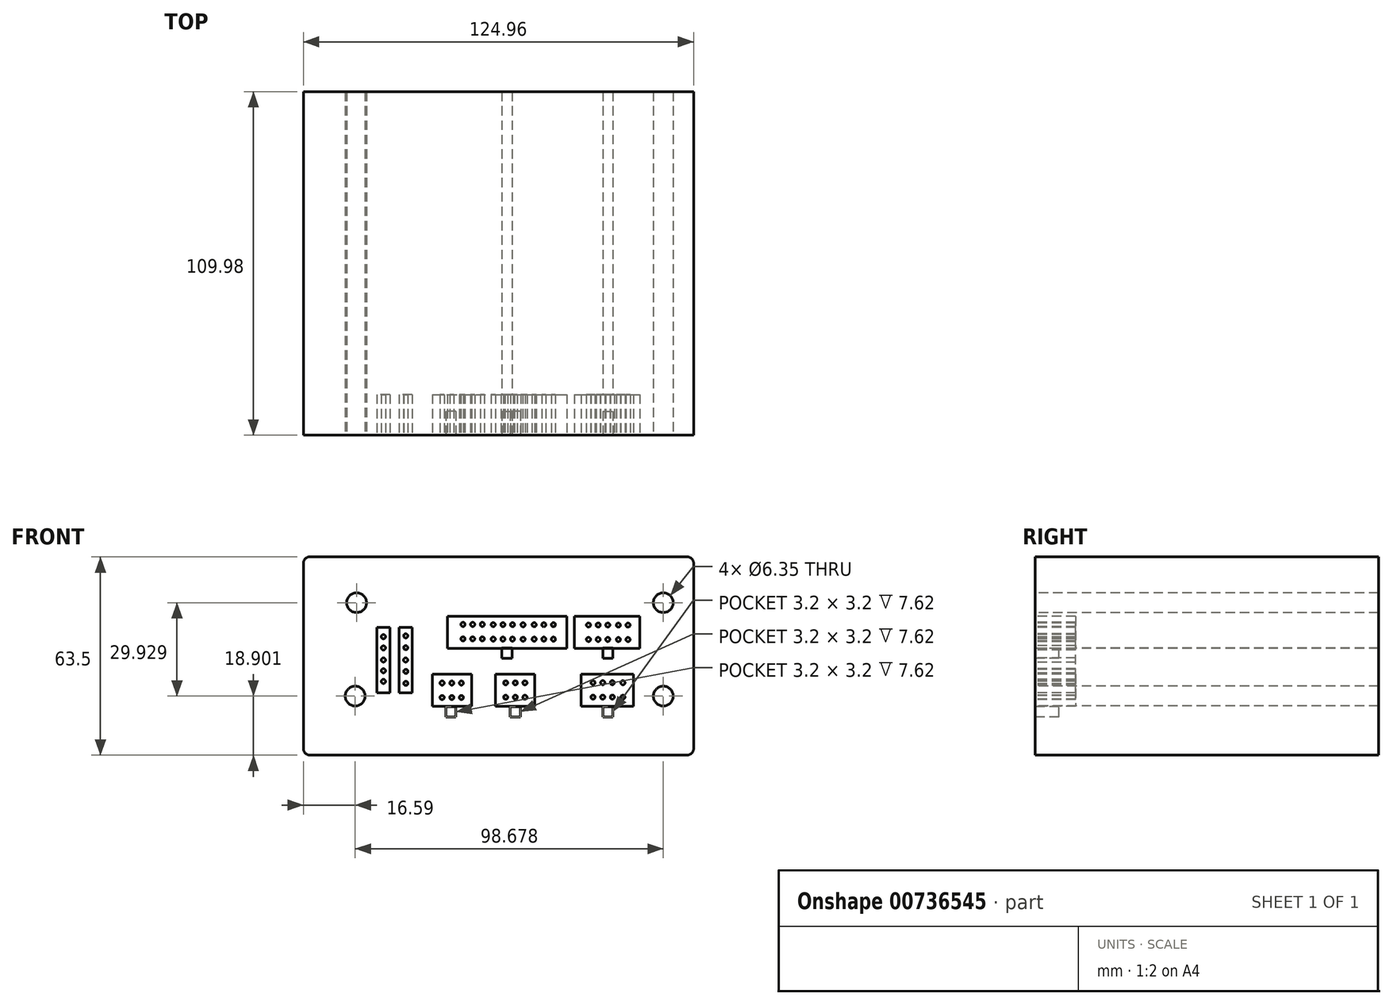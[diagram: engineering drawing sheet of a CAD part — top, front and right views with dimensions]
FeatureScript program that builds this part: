
annotation { "Feature Type Name" : "Feature", "Feature Type Description" : "" }
export const myFeature = defineFeature(function(context is Context, id is Id, definition is map)
    precondition{}
    {
        {
            var Q0;
            Q0=qCreatedBy(makeId("Front.planeOp"),FACE);
            var sketch = newSketch(context, id + "F0", { "sketchPlane" : qUnion([Q0])});
            skLineSegment(sketch, "E0.bottom", {"start": v(-62.48, 31.75) * mm, "end": v(62.48, 31.75) * mm});
            skLineSegment(sketch, "E0.top", {"start": v(-62.48, -31.75) * mm, "end": v(62.48, -31.75) * mm});
            skLineSegment(sketch, "E0.left", {"start": v(-62.48, 31.75) * mm, "end": v(-62.48, -31.75) * mm});
            skLineSegment(sketch, "E0.right", {"start": v(62.48, 31.75) * mm, "end": v(62.48, -31.75) * mm});
            skPoint(sketch, "E0.middle", {"position": v(0, 0) * mm});
            skLineSegment(sketch, "E1.bottom", {"start": v(26.4, -5.88) * mm, "end": v(43.2, -5.88) * mm});
            skLineSegment(sketch, "E1.top", {"start": v(26.4, -16.08) * mm, "end": v(43.2, -16.08) * mm});
            skLineSegment(sketch, "E1.left", {"start": v(26.4, -5.88) * mm, "end": v(26.4, -16.08) * mm});
            skLineSegment(sketch, "E1.right", {"start": v(43.2, -5.88) * mm, "end": v(43.2, -16.08) * mm});
            skPoint(sketch, "E1.middle", {"position": v(34.8, -10.98) * mm});
            skLineSegment(sketch, "E2.bottom", {"start": v(24.3, 12.66) * mm, "end": v(45.3, 12.66) * mm});
            skLineSegment(sketch, "E2.top", {"start": v(24.3, 2.46) * mm, "end": v(45.3, 2.46) * mm});
            skLineSegment(sketch, "E2.left", {"start": v(24.3, 12.66) * mm, "end": v(24.3, 2.46) * mm});
            skLineSegment(sketch, "E2.right", {"start": v(45.3, 12.66) * mm, "end": v(45.3, 2.46) * mm});
            skPoint(sketch, "E2.middle", {"position": v(34.8, 7.56) * mm});
            skLineSegment(sketch, "E3.bottom", {"start": v(-16.35, 12.66) * mm, "end": v(21.85, 12.66) * mm});
            skLineSegment(sketch, "E3.top", {"start": v(-16.35, 2.46) * mm, "end": v(21.85, 2.46) * mm});
            skLineSegment(sketch, "E3.left", {"start": v(-16.35, 12.66) * mm, "end": v(-16.35, 2.46) * mm});
            skLineSegment(sketch, "E3.right", {"start": v(21.85, 12.66) * mm, "end": v(21.85, 2.46) * mm});
            skPoint(sketch, "E3.middle", {"position": v(2.75, 7.56) * mm});
            skLineSegment(sketch, "E4.bottom", {"start": v(-0.96, -5.88) * mm, "end": v(11.64, -5.88) * mm});
            skLineSegment(sketch, "E4.top", {"start": v(-0.96, -16.08) * mm, "end": v(11.64, -16.08) * mm});
            skLineSegment(sketch, "E4.left", {"start": v(-0.96, -5.88) * mm, "end": v(-0.96, -16.08) * mm});
            skLineSegment(sketch, "E4.right", {"start": v(11.64, -5.88) * mm, "end": v(11.64, -16.08) * mm});
            skPoint(sketch, "E4.middle", {"position": v(5.34, -10.98) * mm});
            skLineSegment(sketch, "E5.bottom", {"start": v(-21.23, -5.88) * mm, "end": v(-8.63, -5.88) * mm});
            skLineSegment(sketch, "E5.top", {"start": v(-21.23, -16.08) * mm, "end": v(-8.63, -16.08) * mm});
            skLineSegment(sketch, "E5.left", {"start": v(-21.23, -5.88) * mm, "end": v(-21.23, -16.08) * mm});
            skLineSegment(sketch, "E5.right", {"start": v(-8.63, -5.88) * mm, "end": v(-8.63, -16.08) * mm});
            skPoint(sketch, "E5.middle", {"position": v(-14.93, -10.98) * mm});
            skLineSegment(sketch, "E6.bottom", {"start": v(-27.64, -11.8) * mm, "end": v(-31.84, -11.8) * mm});
            skLineSegment(sketch, "E6.top", {"start": v(-27.64, 9.2) * mm, "end": v(-31.84, 9.2) * mm});
            skLineSegment(sketch, "E6.left", {"start": v(-27.64, -11.8) * mm, "end": v(-27.64, 9.2) * mm});
            skLineSegment(sketch, "E6.right", {"start": v(-31.84, -11.8) * mm, "end": v(-31.84, 9.2) * mm});
            skPoint(sketch, "E6.middle", {"position": v(-29.74, -1.3) * mm});
            skLineSegment(sketch, "E7.bottom", {"start": v(-34.75, -11.8) * mm, "end": v(-38.95, -11.8) * mm});
            skLineSegment(sketch, "E7.top", {"start": v(-34.75, 9.2) * mm, "end": v(-38.95, 9.2) * mm});
            skLineSegment(sketch, "E7.left", {"start": v(-34.75, -11.8) * mm, "end": v(-34.75, 9.2) * mm});
            skLineSegment(sketch, "E7.right", {"start": v(-38.95, -11.8) * mm, "end": v(-38.95, 9.2) * mm});
            skPoint(sketch, "E7.middle", {"position": v(-36.85, -1.3) * mm});
            skLineSegment(sketch, "E8.bottom", {"start": v(36.58, -0.7) * mm, "end": v(33.38, -0.7) * mm});
            skLineSegment(sketch, "E8.top", {"start": v(36.58, 2.5) * mm, "end": v(33.38, 2.5) * mm});
            skLineSegment(sketch, "E8.left", {"start": v(36.58, -0.7) * mm, "end": v(36.58, 2.5) * mm});
            skLineSegment(sketch, "E8.right", {"start": v(33.38, -0.7) * mm, "end": v(33.38, 2.5) * mm});
            skPoint(sketch, "E8.middle", {"position": v(34.98, 0.9) * mm});
            skLineSegment(sketch, "E9.bottom", {"start": v(4.3, -0.7) * mm, "end": v(1.1, -0.7) * mm});
            skLineSegment(sketch, "E9.top", {"start": v(4.3, 2.5) * mm, "end": v(1.1, 2.5) * mm});
            skLineSegment(sketch, "E9.left", {"start": v(4.3, -0.7) * mm, "end": v(4.3, 2.5) * mm});
            skLineSegment(sketch, "E9.right", {"start": v(1.1, -0.7) * mm, "end": v(1.1, 2.5) * mm});
            skPoint(sketch, "E9.middle", {"position": v(2.7, 0.9) * mm});
            skLineSegment(sketch, "E10.bottom", {"start": v(36.58, -19.49) * mm, "end": v(33.38, -19.49) * mm});
            skLineSegment(sketch, "E10.top", {"start": v(36.58, -16.29) * mm, "end": v(33.38, -16.29) * mm});
            skLineSegment(sketch, "E10.left", {"start": v(36.58, -19.49) * mm, "end": v(36.58, -16.29) * mm});
            skLineSegment(sketch, "E10.right", {"start": v(33.38, -19.49) * mm, "end": v(33.38, -16.29) * mm});
            skPoint(sketch, "E10.middle", {"position": v(34.98, -17.89) * mm});
            skLineSegment(sketch, "E11.bottom", {"start": v(6.97, -19.49) * mm, "end": v(3.77, -19.49) * mm});
            skLineSegment(sketch, "E11.top", {"start": v(6.97, -16.29) * mm, "end": v(3.77, -16.29) * mm});
            skLineSegment(sketch, "E11.left", {"start": v(6.97, -19.49) * mm, "end": v(6.97, -16.29) * mm});
            skLineSegment(sketch, "E11.right", {"start": v(3.77, -19.49) * mm, "end": v(3.77, -16.29) * mm});
            skPoint(sketch, "E11.middle", {"position": v(5.37, -17.89) * mm});
            skLineSegment(sketch, "E12.bottom", {"start": v(-13.62, -19.49) * mm, "end": v(-16.82, -19.49) * mm});
            skLineSegment(sketch, "E12.top", {"start": v(-13.62, -16.29) * mm, "end": v(-16.82, -16.29) * mm});
            skLineSegment(sketch, "E12.left", {"start": v(-13.62, -19.49) * mm, "end": v(-13.62, -16.29) * mm});
            skLineSegment(sketch, "E12.right", {"start": v(-16.82, -19.49) * mm, "end": v(-16.82, -16.29) * mm});
            skPoint(sketch, "E12.middle", {"position": v(-15.22, -17.89) * mm});
            skCircle(sketch, "E13", {"center": v(52.79, 17.08) * mm, "radius": 2.62 * mm});
            skCircle(sketch, "E14", {"center": v(52.79, -12.85) * mm, "radius": 2.62 * mm});
            skCircle(sketch, "E15", {"center": v(-45.45, 17.08) * mm, "radius": 2.62 * mm});
            skCircle(sketch, "E16", {"center": v(-45.9, -12.85) * mm, "radius": 2.62 * mm});
            skLineSegment(sketch, "E17.bottom", {"start": v(-61, 13.38) * mm, "end": v(-49.74, 13.38) * mm});
            skLineSegment(sketch, "E17.top", {"start": v(-61, -18.63) * mm, "end": v(-49.74, -18.63) * mm});
            skLineSegment(sketch, "E17.left", {"start": v(-61, 13.38) * mm, "end": v(-61, -18.63) * mm});
            skLineSegment(sketch, "E17.right", {"start": v(-49.74, 13.38) * mm, "end": v(-49.74, -18.63) * mm});
            skPoint(sketch, "E17.middle", {"position": v(-55.37, -2.63) * mm});
            skCircle(sketch, "E18", {"center": v(5.4, -8.6) * mm, "radius": 0.67 * mm});
            skCircle(sketch, "E19", {"center": v(5.4, -13.22) * mm, "radius": 0.67 * mm});
            skCircle(sketch, "E20", {"center": v(8.48, -8.6) * mm, "radius": 0.67 * mm});
            skCircle(sketch, "E21", {"center": v(8.48, -13.22) * mm, "radius": 0.67 * mm});
            skCircle(sketch, "E22", {"center": v(2.3, -8.6) * mm, "radius": 0.67 * mm});
            skCircle(sketch, "E23", {"center": v(2.3, -13.22) * mm, "radius": 0.67 * mm});
            skCircle(sketch, "E24", {"center": v(-14.96, -8.66) * mm, "radius": 0.67 * mm});
            skCircle(sketch, "E25", {"center": v(-14.96, -13.29) * mm, "radius": 0.67 * mm});
            skCircle(sketch, "E26", {"center": v(-11.88, -8.66) * mm, "radius": 0.67 * mm});
            skCircle(sketch, "E27", {"center": v(-11.88, -13.29) * mm, "radius": 0.67 * mm});
            skCircle(sketch, "E28", {"center": v(-18.06, -8.66) * mm, "radius": 0.67 * mm});
            skCircle(sketch, "E29", {"center": v(-18.06, -13.29) * mm, "radius": 0.67 * mm});
            skCircle(sketch, "E30", {"center": v(31.93, 9.92) * mm, "radius": 0.67 * mm});
            skCircle(sketch, "E31", {"center": v(31.93, 5.3) * mm, "radius": 0.67 * mm});
            skCircle(sketch, "E32", {"center": v(35, 9.92) * mm, "radius": 0.67 * mm});
            skCircle(sketch, "E33", {"center": v(35, 5.3) * mm, "radius": 0.67 * mm});
            skCircle(sketch, "E34", {"center": v(28.83, 9.92) * mm, "radius": 0.67 * mm});
            skCircle(sketch, "E35", {"center": v(28.83, 5.3) * mm, "radius": 0.67 * mm});
            skCircle(sketch, "E36", {"center": v(41.48, 9.9) * mm, "radius": 0.67 * mm});
            skCircle(sketch, "E37", {"center": v(41.48, 5.27) * mm, "radius": 0.67 * mm});
            skCircle(sketch, "E38", {"center": v(38.38, 9.9) * mm, "radius": 0.67 * mm});
            skCircle(sketch, "E39", {"center": v(38.38, 5.27) * mm, "radius": 0.67 * mm});
            skCircle(sketch, "E40", {"center": v(33.38, -8.54) * mm, "radius": 0.67 * mm});
            skCircle(sketch, "E41", {"center": v(33.38, -13.16) * mm, "radius": 0.67 * mm});
            skCircle(sketch, "E42", {"center": v(36.46, -8.54) * mm, "radius": 0.67 * mm});
            skCircle(sketch, "E43", {"center": v(36.46, -13.16) * mm, "radius": 0.67 * mm});
            skCircle(sketch, "E44", {"center": v(30.28, -8.54) * mm, "radius": 0.67 * mm});
            skCircle(sketch, "E45", {"center": v(30.28, -13.16) * mm, "radius": 0.67 * mm});
            skCircle(sketch, "E46", {"center": v(39.84, -8.57) * mm, "radius": 0.67 * mm});
            skCircle(sketch, "E47", {"center": v(39.84, -13.2) * mm, "radius": 0.67 * mm});
            skCircle(sketch, "E48", {"center": v(1.41, 10.03) * mm, "radius": 0.67 * mm});
            skCircle(sketch, "E49", {"center": v(1.41, 5.4) * mm, "radius": 0.67 * mm});
            skCircle(sketch, "E50", {"center": v(4.5, 10.03) * mm, "radius": 0.67 * mm});
            skCircle(sketch, "E51", {"center": v(4.5, 5.4) * mm, "radius": 0.67 * mm});
            skCircle(sketch, "E52", {"center": v(-1.69, 10.03) * mm, "radius": 0.67 * mm});
            skCircle(sketch, "E53", {"center": v(-1.69, 5.4) * mm, "radius": 0.67 * mm});
            skCircle(sketch, "E54", {"center": v(7.87, 10) * mm, "radius": 0.67 * mm});
            skCircle(sketch, "E55", {"center": v(7.87, 5.38) * mm, "radius": 0.67 * mm});
            skCircle(sketch, "E56", {"center": v(14.52, 10.02) * mm, "radius": 0.67 * mm});
            skCircle(sketch, "E57", {"center": v(14.52, 5.4) * mm, "radius": 0.67 * mm});
            skCircle(sketch, "E58", {"center": v(17.6, 10.02) * mm, "radius": 0.67 * mm});
            skCircle(sketch, "E59", {"center": v(17.6, 5.4) * mm, "radius": 0.67 * mm});
            skCircle(sketch, "E60", {"center": v(11.42, 10.02) * mm, "radius": 0.67 * mm});
            skCircle(sketch, "E61", {"center": v(11.42, 5.4) * mm, "radius": 0.67 * mm});
            skCircle(sketch, "E62", {"center": v(-8.27, 10.11) * mm, "radius": 0.67 * mm});
            skCircle(sketch, "E63", {"center": v(-8.27, 5.49) * mm, "radius": 0.67 * mm});
            skCircle(sketch, "E64", {"center": v(-5.19, 10.11) * mm, "radius": 0.67 * mm});
            skCircle(sketch, "E65", {"center": v(-5.19, 5.49) * mm, "radius": 0.67 * mm});
            skCircle(sketch, "E66", {"center": v(-11.37, 10.11) * mm, "radius": 0.67 * mm});
            skCircle(sketch, "E67", {"center": v(-11.37, 5.49) * mm, "radius": 0.67 * mm});
            skCircle(sketch, "E68", {"center": v(97.44, -13.64) * mm, "radius": 0.67 * mm});
            skCircle(sketch, "E69", {"center": v(97.44, -18.27) * mm, "radius": 0.67 * mm});
            skCircle(sketch, "E70", {"center": v(-29.7, 6.45) * mm, "radius": 0.67 * mm});
            skCircle(sketch, "E71", {"center": v(-29.7, 2.66) * mm, "radius": 0.67 * mm});
            skCircle(sketch, "E72", {"center": v(-29.74, -1.3) * mm, "radius": 0.67 * mm});
            skPoint(sketch, "E73.middle", {"position": v(-29.67, -4.94) * mm});
            skCircle(sketch, "E74", {"center": v(-29.67, -4.94) * mm, "radius": 0.67 * mm});
            skPoint(sketch, "E75.middle", {"position": v(-29.67, -8.77) * mm});
            skCircle(sketch, "E76", {"center": v(-29.67, -8.77) * mm, "radius": 0.67 * mm});
            skCircle(sketch, "E77", {"center": v(-36.85, -1.3) * mm, "radius": 0.67 * mm});
            skPoint(sketch, "E78.middle", {"position": v(-36.85, 2.6) * mm});
            skCircle(sketch, "E79", {"center": v(-36.85, 2.6) * mm, "radius": 0.67 * mm});
            skPoint(sketch, "E80.middle", {"position": v(-36.85, 6.18) * mm});
            skCircle(sketch, "E81", {"center": v(-36.85, 6.18) * mm, "radius": 0.67 * mm});
            skPoint(sketch, "E82.middle", {"position": v(-36.85, -4.73) * mm});
            skCircle(sketch, "E83", {"center": v(-36.85, -4.73) * mm, "radius": 0.67 * mm});
            skPoint(sketch, "E84.middle", {"position": v(-36.85, -8.15) * mm});
            skCircle(sketch, "E85", {"center": v(-36.85, -8.15) * mm, "radius": 0.67 * mm});
            skSolve(sketch);
        }
        {
            var Q0;
            Q0=makeQuery(id+"F0.imprint","IMPRINT",FACE,{"disambiguationData":[TD([[makeQuery(id+"F0.imprint","IMPRINT",EDGE,{"derivedFrom":sQuery(id+"F0.wireOp",EDGE,"E0.bottom")}),-1.0]])]});
            var Q1;
            Q1=makeQuery(id+"F0.imprint","IMPRINT",FACE,{"disambiguationData":[TD([[makeQuery(id+"F0.imprint","IMPRINT",EDGE,{"derivedFrom":sQuery(id+"F0.wireOp",EDGE,"E3.bottom")}),-1.0]])]});
            var Q2;
            Q2=makeQuery(id+"F0.imprint","IMPRINT",FACE,{"disambiguationData":[TD([[makeQuery(id+"F0.imprint","IMPRINT",EDGE,{"derivedFrom":sQuery(id+"F0.wireOp",EDGE,"E2.bottom")}),-1.0]])]});
            var Q3;
            Q3=makeQuery(id+"F0.imprint","IMPRINT",FACE,{"disambiguationData":[TD([[makeQuery(id+"F0.imprint","IMPRINT",EDGE,{"derivedFrom":sQuery(id+"F0.wireOp",EDGE,"E10.bottom")}),-1.0]])]});
            var Q4;
            Q4=makeQuery(id+"F0.imprint","IMPRINT",FACE,{"disambiguationData":[TD([[makeQuery(id+"F0.imprint","IMPRINT",EDGE,{"derivedFrom":sQuery(id+"F0.wireOp",EDGE,"E4.bottom")}),-1.0]])]});
            var Q5;
            Q5=makeQuery(id+"F0.imprint","IMPRINT",FACE,{"disambiguationData":[TD([[makeQuery(id+"F0.imprint","IMPRINT",EDGE,{"derivedFrom":sQuery(id+"F0.wireOp",EDGE,"E11.bottom")}),-1.0]])]});
            var Q6;
            Q6=makeQuery(id+"F0.imprint","IMPRINT",FACE,{"disambiguationData":[TD([[makeQuery(id+"F0.imprint","IMPRINT",EDGE,{"derivedFrom":sQuery(id+"F0.wireOp",EDGE,"E1.bottom")}),-1.0]])]});
            var Q7;
            Q7=makeQuery(id+"F0.imprint","IMPRINT",FACE,{"disambiguationData":[TD([[makeQuery(id+"F0.imprint","IMPRINT",EDGE,{"derivedFrom":sQuery(id+"F0.wireOp",EDGE,"E5.bottom")}),-1.0]])]});
            var Q8;
            Q8=makeQuery(id+"F0.imprint","IMPRINT",FACE,{"disambiguationData":[TD([[makeQuery(id+"F0.imprint","IMPRINT",EDGE,{"derivedFrom":sQuery(id+"F0.wireOp",EDGE,"E12.bottom")}),-1.0]])]});
            var Q9;
            Q9=makeQuery(id+"F0.imprint","IMPRINT",FACE,{"disambiguationData":[TD([[makeQuery(id+"F0.imprint","IMPRINT",EDGE,{"derivedFrom":sQuery(id+"F0.wireOp",EDGE,"E6.bottom")}),-1.0]])]});
            var Q10;
            Q10=makeQuery(id+"F0.imprint","IMPRINT",FACE,{"disambiguationData":[TD([[makeQuery(id+"F0.imprint","IMPRINT",EDGE,{"derivedFrom":sQuery(id+"F0.wireOp",EDGE,"E7.bottom")}),-1.0]])]});
            var Q11;
            Q11=makeQuery(id+"F0.imprint","IMPRINT",FACE,{"disambiguationData":[TD([[makeQuery(id+"F0.imprint","IMPRINT",EDGE,{"derivedFrom":sQuery(id+"F0.wireOp",EDGE,"E17.bottom")}),-1.0]])]});
            var Q12;
            Q12=makeQuery(id+"F0.imprint","IMPRINT",FACE,{"disambiguationData":[TD([[makeQuery(id+"F0.imprint","IMPRINT",EDGE,{"derivedFrom":sQuery(id+"F0.wireOp",EDGE,"E15")}),1.0]])]});
            var Q13;
            Q13=makeQuery(id+"F0.imprint","IMPRINT",FACE,{"disambiguationData":[TD([[makeQuery(id+"F0.imprint","IMPRINT",EDGE,{"derivedFrom":sQuery(id+"F0.wireOp",EDGE,"E16")}),1.0]])]});
            var Q14;
            Q14=makeQuery(id+"F0.imprint","IMPRINT",FACE,{"disambiguationData":[TD([[makeQuery(id+"F0.imprint","IMPRINT",EDGE,{"derivedFrom":sQuery(id+"F0.wireOp",EDGE,"E14")}),1.0]])]});
            var Q15;
            Q15=makeQuery(id+"F0.imprint","IMPRINT",FACE,{"disambiguationData":[TD([[makeQuery(id+"F0.imprint","IMPRINT",EDGE,{"derivedFrom":sQuery(id+"F0.wireOp",EDGE,"E13")}),1.0]])]});
            var Q16;
            {var subQ5=sQuery(id+"F0.wireOp",EDGE,"E8.bottom");Q16=makeQuery(id+"F0.imprint","IMPRINT",FACE,{"disambiguationData":[TD([[makeQuery(id+"F0.imprint","IMPRINT",EDGE,{"derivedFrom":subQ5}),-1.0]])]});}
            var Q17;
            {var subQ5=sQuery(id+"F0.wireOp",EDGE,"E9.bottom");Q17=makeQuery(id+"F0.imprint","IMPRINT",FACE,{"disambiguationData":[TD([[makeQuery(id+"F0.imprint","IMPRINT",EDGE,{"derivedFrom":subQ5}),-1.0]])]});}
            var Q18;
            Q18=makeQuery(id+"F0.imprint","IMPRINT",FACE,{"disambiguationData":[TD([[makeQuery(id+"F0.imprint","IMPRINT",EDGE,{"derivedFrom":sQuery(id+"F0.wireOp",EDGE,"E81")}),1.0]])]});
            var Q19;
            Q19=makeQuery(id+"F0.imprint","IMPRINT",FACE,{"disambiguationData":[TD([[makeQuery(id+"F0.imprint","IMPRINT",EDGE,{"derivedFrom":sQuery(id+"F0.wireOp",EDGE,"E79")}),1.0]])]});
            var Q20;
            Q20=makeQuery(id+"F0.imprint","IMPRINT",FACE,{"disambiguationData":[TD([[makeQuery(id+"F0.imprint","IMPRINT",EDGE,{"derivedFrom":sQuery(id+"F0.wireOp",EDGE,"E77")}),1.0]])]});
            var Q21;
            Q21=makeQuery(id+"F0.imprint","IMPRINT",FACE,{"disambiguationData":[TD([[makeQuery(id+"F0.imprint","IMPRINT",EDGE,{"derivedFrom":sQuery(id+"F0.wireOp",EDGE,"E83")}),1.0]])]});
            var Q22;
            Q22=makeQuery(id+"F0.imprint","IMPRINT",FACE,{"disambiguationData":[TD([[makeQuery(id+"F0.imprint","IMPRINT",EDGE,{"derivedFrom":sQuery(id+"F0.wireOp",EDGE,"E85")}),1.0]])]});
            var Q23;
            Q23=makeQuery(id+"F0.imprint","IMPRINT",FACE,{"disambiguationData":[TD([[makeQuery(id+"F0.imprint","IMPRINT",EDGE,{"derivedFrom":sQuery(id+"F0.wireOp",EDGE,"E76")}),1.0]])]});
            var Q24;
            Q24=makeQuery(id+"F0.imprint","IMPRINT",FACE,{"disambiguationData":[TD([[makeQuery(id+"F0.imprint","IMPRINT",EDGE,{"derivedFrom":sQuery(id+"F0.wireOp",EDGE,"E74")}),1.0]])]});
            var Q25;
            Q25=makeQuery(id+"F0.imprint","IMPRINT",FACE,{"disambiguationData":[TD([[makeQuery(id+"F0.imprint","IMPRINT",EDGE,{"derivedFrom":sQuery(id+"F0.wireOp",EDGE,"E72")}),1.0]])]});
            var Q26;
            Q26=makeQuery(id+"F0.imprint","IMPRINT",FACE,{"disambiguationData":[TD([[makeQuery(id+"F0.imprint","IMPRINT",EDGE,{"derivedFrom":sQuery(id+"F0.wireOp",EDGE,"E71")}),1.0]])]});
            var Q27;
            Q27=makeQuery(id+"F0.imprint","IMPRINT",FACE,{"disambiguationData":[TD([[makeQuery(id+"F0.imprint","IMPRINT",EDGE,{"derivedFrom":sQuery(id+"F0.wireOp",EDGE,"E70")}),1.0]])]});
            var Q28;
            Q28=makeQuery(id+"F0.imprint","IMPRINT",FACE,{"disambiguationData":[TD([[makeQuery(id+"F0.imprint","IMPRINT",EDGE,{"derivedFrom":sQuery(id+"F0.wireOp",EDGE,"E28")}),1.0]])]});
            var Q29;
            Q29=makeQuery(id+"F0.imprint","IMPRINT",FACE,{"disambiguationData":[TD([[makeQuery(id+"F0.imprint","IMPRINT",EDGE,{"derivedFrom":sQuery(id+"F0.wireOp",EDGE,"E24")}),1.0]])]});
            var Q30;
            Q30=makeQuery(id+"F0.imprint","IMPRINT",FACE,{"disambiguationData":[TD([[makeQuery(id+"F0.imprint","IMPRINT",EDGE,{"derivedFrom":sQuery(id+"F0.wireOp",EDGE,"E26")}),1.0]])]});
            var Q31;
            Q31=makeQuery(id+"F0.imprint","IMPRINT",FACE,{"disambiguationData":[TD([[makeQuery(id+"F0.imprint","IMPRINT",EDGE,{"derivedFrom":sQuery(id+"F0.wireOp",EDGE,"E27")}),1.0]])]});
            var Q32;
            Q32=makeQuery(id+"F0.imprint","IMPRINT",FACE,{"disambiguationData":[TD([[makeQuery(id+"F0.imprint","IMPRINT",EDGE,{"derivedFrom":sQuery(id+"F0.wireOp",EDGE,"E25")}),1.0]])]});
            var Q33;
            Q33=makeQuery(id+"F0.imprint","IMPRINT",FACE,{"disambiguationData":[TD([[makeQuery(id+"F0.imprint","IMPRINT",EDGE,{"derivedFrom":sQuery(id+"F0.wireOp",EDGE,"E29")}),1.0]])]});
            var Q34;
            Q34=makeQuery(id+"F0.imprint","IMPRINT",FACE,{"disambiguationData":[TD([[makeQuery(id+"F0.imprint","IMPRINT",EDGE,{"derivedFrom":sQuery(id+"F0.wireOp",EDGE,"E22")}),1.0]])]});
            var Q35;
            Q35=makeQuery(id+"F0.imprint","IMPRINT",FACE,{"disambiguationData":[TD([[makeQuery(id+"F0.imprint","IMPRINT",EDGE,{"derivedFrom":sQuery(id+"F0.wireOp",EDGE,"E18")}),1.0]])]});
            var Q36;
            Q36=makeQuery(id+"F0.imprint","IMPRINT",FACE,{"disambiguationData":[TD([[makeQuery(id+"F0.imprint","IMPRINT",EDGE,{"derivedFrom":sQuery(id+"F0.wireOp",EDGE,"E20")}),1.0]])]});
            var Q37;
            Q37=makeQuery(id+"F0.imprint","IMPRINT",FACE,{"disambiguationData":[TD([[makeQuery(id+"F0.imprint","IMPRINT",EDGE,{"derivedFrom":sQuery(id+"F0.wireOp",EDGE,"E21")}),1.0]])]});
            var Q38;
            Q38=makeQuery(id+"F0.imprint","IMPRINT",FACE,{"disambiguationData":[TD([[makeQuery(id+"F0.imprint","IMPRINT",EDGE,{"derivedFrom":sQuery(id+"F0.wireOp",EDGE,"E19")}),1.0]])]});
            var Q39;
            Q39=makeQuery(id+"F0.imprint","IMPRINT",FACE,{"disambiguationData":[TD([[makeQuery(id+"F0.imprint","IMPRINT",EDGE,{"derivedFrom":sQuery(id+"F0.wireOp",EDGE,"E23")}),1.0]])]});
            var Q40;
            Q40=makeQuery(id+"F0.imprint","IMPRINT",FACE,{"disambiguationData":[TD([[makeQuery(id+"F0.imprint","IMPRINT",EDGE,{"derivedFrom":sQuery(id+"F0.wireOp",EDGE,"E66")}),1.0]])]});
            var Q41;
            Q41=makeQuery(id+"F0.imprint","IMPRINT",FACE,{"disambiguationData":[TD([[makeQuery(id+"F0.imprint","IMPRINT",EDGE,{"derivedFrom":sQuery(id+"F0.wireOp",EDGE,"E67")}),1.0]])]});
            var Q42;
            Q42=makeQuery(id+"F0.imprint","IMPRINT",FACE,{"disambiguationData":[TD([[makeQuery(id+"F0.imprint","IMPRINT",EDGE,{"derivedFrom":sQuery(id+"F0.wireOp",EDGE,"E63")}),1.0]])]});
            var Q43;
            Q43=makeQuery(id+"F0.imprint","IMPRINT",FACE,{"disambiguationData":[TD([[makeQuery(id+"F0.imprint","IMPRINT",EDGE,{"derivedFrom":sQuery(id+"F0.wireOp",EDGE,"E62")}),1.0]])]});
            var Q44;
            Q44=makeQuery(id+"F0.imprint","IMPRINT",FACE,{"disambiguationData":[TD([[makeQuery(id+"F0.imprint","IMPRINT",EDGE,{"derivedFrom":sQuery(id+"F0.wireOp",EDGE,"E64")}),1.0]])]});
            var Q45;
            Q45=makeQuery(id+"F0.imprint","IMPRINT",FACE,{"disambiguationData":[TD([[makeQuery(id+"F0.imprint","IMPRINT",EDGE,{"derivedFrom":sQuery(id+"F0.wireOp",EDGE,"E65")}),1.0]])]});
            var Q46;
            Q46=makeQuery(id+"F0.imprint","IMPRINT",FACE,{"disambiguationData":[TD([[makeQuery(id+"F0.imprint","IMPRINT",EDGE,{"derivedFrom":sQuery(id+"F0.wireOp",EDGE,"E53")}),1.0]])]});
            var Q47;
            Q47=makeQuery(id+"F0.imprint","IMPRINT",FACE,{"disambiguationData":[TD([[makeQuery(id+"F0.imprint","IMPRINT",EDGE,{"derivedFrom":sQuery(id+"F0.wireOp",EDGE,"E52")}),1.0]])]});
            var Q48;
            Q48=makeQuery(id+"F0.imprint","IMPRINT",FACE,{"disambiguationData":[TD([[makeQuery(id+"F0.imprint","IMPRINT",EDGE,{"derivedFrom":sQuery(id+"F0.wireOp",EDGE,"E48")}),1.0]])]});
            var Q49;
            Q49=makeQuery(id+"F0.imprint","IMPRINT",FACE,{"disambiguationData":[TD([[makeQuery(id+"F0.imprint","IMPRINT",EDGE,{"derivedFrom":sQuery(id+"F0.wireOp",EDGE,"E49")}),1.0]])]});
            var Q50;
            Q50=makeQuery(id+"F0.imprint","IMPRINT",FACE,{"disambiguationData":[TD([[makeQuery(id+"F0.imprint","IMPRINT",EDGE,{"derivedFrom":sQuery(id+"F0.wireOp",EDGE,"E51")}),1.0]])]});
            var Q51;
            Q51=makeQuery(id+"F0.imprint","IMPRINT",FACE,{"disambiguationData":[TD([[makeQuery(id+"F0.imprint","IMPRINT",EDGE,{"derivedFrom":sQuery(id+"F0.wireOp",EDGE,"E50")}),1.0]])]});
            var Q52;
            Q52=makeQuery(id+"F0.imprint","IMPRINT",FACE,{"disambiguationData":[TD([[makeQuery(id+"F0.imprint","IMPRINT",EDGE,{"derivedFrom":sQuery(id+"F0.wireOp",EDGE,"E54")}),1.0]])]});
            var Q53;
            Q53=makeQuery(id+"F0.imprint","IMPRINT",FACE,{"disambiguationData":[TD([[makeQuery(id+"F0.imprint","IMPRINT",EDGE,{"derivedFrom":sQuery(id+"F0.wireOp",EDGE,"E61")}),1.0]])]});
            var Q54;
            Q54=makeQuery(id+"F0.imprint","IMPRINT",FACE,{"disambiguationData":[TD([[makeQuery(id+"F0.imprint","IMPRINT",EDGE,{"derivedFrom":sQuery(id+"F0.wireOp",EDGE,"E60")}),1.0]])]});
            var Q55;
            Q55=makeQuery(id+"F0.imprint","IMPRINT",FACE,{"disambiguationData":[TD([[makeQuery(id+"F0.imprint","IMPRINT",EDGE,{"derivedFrom":sQuery(id+"F0.wireOp",EDGE,"E56")}),1.0]])]});
            var Q56;
            Q56=makeQuery(id+"F0.imprint","IMPRINT",FACE,{"disambiguationData":[TD([[makeQuery(id+"F0.imprint","IMPRINT",EDGE,{"derivedFrom":sQuery(id+"F0.wireOp",EDGE,"E59")}),1.0]])]});
            var Q57;
            Q57=makeQuery(id+"F0.imprint","IMPRINT",FACE,{"disambiguationData":[TD([[makeQuery(id+"F0.imprint","IMPRINT",EDGE,{"derivedFrom":sQuery(id+"F0.wireOp",EDGE,"E58")}),1.0]])]});
            var Q58;
            Q58=makeQuery(id+"F0.imprint","IMPRINT",FACE,{"disambiguationData":[TD([[makeQuery(id+"F0.imprint","IMPRINT",EDGE,{"derivedFrom":sQuery(id+"F0.wireOp",EDGE,"E55")}),1.0]])]});
            var Q59;
            Q59=makeQuery(id+"F0.imprint","IMPRINT",FACE,{"disambiguationData":[TD([[makeQuery(id+"F0.imprint","IMPRINT",EDGE,{"derivedFrom":sQuery(id+"F0.wireOp",EDGE,"E57")}),1.0]])]});
            var Q60;
            Q60=makeQuery(id+"F0.imprint","IMPRINT",FACE,{"disambiguationData":[TD([[makeQuery(id+"F0.imprint","IMPRINT",EDGE,{"derivedFrom":sQuery(id+"F0.wireOp",EDGE,"E34")}),1.0]])]});
            var Q61;
            Q61=makeQuery(id+"F0.imprint","IMPRINT",FACE,{"disambiguationData":[TD([[makeQuery(id+"F0.imprint","IMPRINT",EDGE,{"derivedFrom":sQuery(id+"F0.wireOp",EDGE,"E30")}),1.0]])]});
            var Q62;
            Q62=makeQuery(id+"F0.imprint","IMPRINT",FACE,{"disambiguationData":[TD([[makeQuery(id+"F0.imprint","IMPRINT",EDGE,{"derivedFrom":sQuery(id+"F0.wireOp",EDGE,"E32")}),1.0]])]});
            var Q63;
            Q63=makeQuery(id+"F0.imprint","IMPRINT",FACE,{"disambiguationData":[TD([[makeQuery(id+"F0.imprint","IMPRINT",EDGE,{"derivedFrom":sQuery(id+"F0.wireOp",EDGE,"E38")}),1.0]])]});
            var Q64;
            Q64=makeQuery(id+"F0.imprint","IMPRINT",FACE,{"disambiguationData":[TD([[makeQuery(id+"F0.imprint","IMPRINT",EDGE,{"derivedFrom":sQuery(id+"F0.wireOp",EDGE,"E36")}),1.0]])]});
            var Q65;
            Q65=makeQuery(id+"F0.imprint","IMPRINT",FACE,{"disambiguationData":[TD([[makeQuery(id+"F0.imprint","IMPRINT",EDGE,{"derivedFrom":sQuery(id+"F0.wireOp",EDGE,"E37")}),1.0]])]});
            var Q66;
            Q66=makeQuery(id+"F0.imprint","IMPRINT",FACE,{"disambiguationData":[TD([[makeQuery(id+"F0.imprint","IMPRINT",EDGE,{"derivedFrom":sQuery(id+"F0.wireOp",EDGE,"E39")}),1.0]])]});
            var Q67;
            Q67=makeQuery(id+"F0.imprint","IMPRINT",FACE,{"disambiguationData":[TD([[makeQuery(id+"F0.imprint","IMPRINT",EDGE,{"derivedFrom":sQuery(id+"F0.wireOp",EDGE,"E33")}),1.0]])]});
            var Q68;
            Q68=makeQuery(id+"F0.imprint","IMPRINT",FACE,{"disambiguationData":[TD([[makeQuery(id+"F0.imprint","IMPRINT",EDGE,{"derivedFrom":sQuery(id+"F0.wireOp",EDGE,"E31")}),1.0]])]});
            var Q69;
            Q69=makeQuery(id+"F0.imprint","IMPRINT",FACE,{"disambiguationData":[TD([[makeQuery(id+"F0.imprint","IMPRINT",EDGE,{"derivedFrom":sQuery(id+"F0.wireOp",EDGE,"E35")}),1.0]])]});
            var Q70;
            Q70=makeQuery(id+"F0.imprint","IMPRINT",FACE,{"disambiguationData":[TD([[makeQuery(id+"F0.imprint","IMPRINT",EDGE,{"derivedFrom":sQuery(id+"F0.wireOp",EDGE,"E46")}),1.0]])]});
            var Q71;
            Q71=makeQuery(id+"F0.imprint","IMPRINT",FACE,{"disambiguationData":[TD([[makeQuery(id+"F0.imprint","IMPRINT",EDGE,{"derivedFrom":sQuery(id+"F0.wireOp",EDGE,"E42")}),1.0]])]});
            var Q72;
            Q72=makeQuery(id+"F0.imprint","IMPRINT",FACE,{"disambiguationData":[TD([[makeQuery(id+"F0.imprint","IMPRINT",EDGE,{"derivedFrom":sQuery(id+"F0.wireOp",EDGE,"E40")}),1.0]])]});
            var Q73;
            Q73=makeQuery(id+"F0.imprint","IMPRINT",FACE,{"disambiguationData":[TD([[makeQuery(id+"F0.imprint","IMPRINT",EDGE,{"derivedFrom":sQuery(id+"F0.wireOp",EDGE,"E44")}),1.0]])]});
            var Q74;
            Q74=makeQuery(id+"F0.imprint","IMPRINT",FACE,{"disambiguationData":[TD([[makeQuery(id+"F0.imprint","IMPRINT",EDGE,{"derivedFrom":sQuery(id+"F0.wireOp",EDGE,"E45")}),1.0]])]});
            var Q75;
            Q75=makeQuery(id+"F0.imprint","IMPRINT",FACE,{"disambiguationData":[TD([[makeQuery(id+"F0.imprint","IMPRINT",EDGE,{"derivedFrom":sQuery(id+"F0.wireOp",EDGE,"E41")}),1.0]])]});
            var Q76;
            Q76=makeQuery(id+"F0.imprint","IMPRINT",FACE,{"disambiguationData":[TD([[makeQuery(id+"F0.imprint","IMPRINT",EDGE,{"derivedFrom":sQuery(id+"F0.wireOp",EDGE,"E43")}),1.0]])]});
            var Q77;
            Q77=makeQuery(id+"F0.imprint","IMPRINT",FACE,{"disambiguationData":[TD([[makeQuery(id+"F0.imprint","IMPRINT",EDGE,{"derivedFrom":sQuery(id+"F0.wireOp",EDGE,"E47")}),1.0]])]});
            extrude(context, id + "F1", {"entities" : qUnion([Q0, Q1, Q2, Q3, Q4, Q5, Q6, Q7, Q8, Q9, Q10, Q11, Q12, Q13, Q14, Q15, Q16, Q17, Q18, Q19, Q20, Q21, Q22, Q23, Q24, Q25, Q26, Q27, Q28, Q29, Q30, Q31, Q32, Q33, Q34, Q35, Q36, Q37, Q38, Q39, Q40, Q41, Q42, Q43, Q44, Q45, Q46, Q47, Q48, Q49, Q50, Q51, Q52, Q53, Q54, Q55, Q56, Q57, Q58, Q59, Q60, Q61, Q62, Q63, Q64, Q65, Q66, Q67, Q68, Q69, Q70, Q71, Q72, Q73, Q74, Q75, Q76, Q77]), "oppositeDirection" : true, "depth" : 109.98 * mm, "offsetDistance" : 25.4 * mm});
        }
        {
            var Q0;
            Q0=makeQuery(id+"F0.imprint","IMPRINT",FACE,{"disambiguationData":[TD([[makeQuery(id+"F0.imprint","IMPRINT",EDGE,{"derivedFrom":sQuery(id+"F0.wireOp",EDGE,"E3.bottom")}),-1.0]])]});
            var Q1;
            Q1=makeQuery(id+"F0.imprint","IMPRINT",FACE,{"disambiguationData":[TD([[makeQuery(id+"F0.imprint","IMPRINT",EDGE,{"derivedFrom":sQuery(id+"F0.wireOp",EDGE,"E2.bottom")}),-1.0]])]});
            var Q2;
            Q2=makeQuery(id+"F0.imprint","IMPRINT",FACE,{"disambiguationData":[TD([[makeQuery(id+"F0.imprint","IMPRINT",EDGE,{"derivedFrom":sQuery(id+"F0.wireOp",EDGE,"E1.bottom")}),-1.0]])]});
            var Q3;
            Q3=makeQuery(id+"F0.imprint","IMPRINT",FACE,{"disambiguationData":[TD([[makeQuery(id+"F0.imprint","IMPRINT",EDGE,{"derivedFrom":sQuery(id+"F0.wireOp",EDGE,"E4.bottom")}),-1.0]])]});
            var Q4;
            Q4=makeQuery(id+"F0.imprint","IMPRINT",FACE,{"disambiguationData":[TD([[makeQuery(id+"F0.imprint","IMPRINT",EDGE,{"derivedFrom":sQuery(id+"F0.wireOp",EDGE,"E5.bottom")}),-1.0]])]});
            var Q5;
            Q5=makeQuery(id+"F0.imprint","IMPRINT",FACE,{"disambiguationData":[TD([[makeQuery(id+"F0.imprint","IMPRINT",EDGE,{"derivedFrom":sQuery(id+"F0.wireOp",EDGE,"E7.bottom")}),-1.0]])]});
            var Q6;
            Q6=makeQuery(id+"F0.imprint","IMPRINT",FACE,{"disambiguationData":[TD([[makeQuery(id+"F0.imprint","IMPRINT",EDGE,{"derivedFrom":sQuery(id+"F0.wireOp",EDGE,"E6.bottom")}),-1.0]])]});
            extrude(context, id + "F2", {"entities" : qUnion([Q0, Q1, Q2, Q3, Q4, Q5, Q6]), "operationType" : NewBodyOperationType.REMOVE, "oppositeDirection" : true, "depth" : 13 * mm, "offsetDistance" : 25.4 * mm});
        }
        {
            var Q0;
            {var subQ5=sQuery(id+"F0.wireOp",EDGE,"E9.bottom");Q0=makeQuery(id+"F0.imprint","IMPRINT",FACE,{"disambiguationData":[TD([[makeQuery(id+"F0.imprint","IMPRINT",EDGE,{"derivedFrom":subQ5}),-1.0]])]});}
            var Q1;
            {var subQ5=sQuery(id+"F0.wireOp",EDGE,"E8.bottom");Q1=makeQuery(id+"F0.imprint","IMPRINT",FACE,{"disambiguationData":[TD([[makeQuery(id+"F0.imprint","IMPRINT",EDGE,{"derivedFrom":subQ5}),-1.0]])]});}
            var Q2;
            Q2=makeQuery(id+"F0.imprint","IMPRINT",FACE,{"disambiguationData":[TD([[makeQuery(id+"F0.imprint","IMPRINT",EDGE,{"derivedFrom":sQuery(id+"F0.wireOp",EDGE,"E10.bottom")}),-1.0]])]});
            var Q3;
            Q3=makeQuery(id+"F0.imprint","IMPRINT",FACE,{"disambiguationData":[TD([[makeQuery(id+"F0.imprint","IMPRINT",EDGE,{"derivedFrom":sQuery(id+"F0.wireOp",EDGE,"E11.bottom")}),-1.0]])]});
            var Q4;
            Q4=makeQuery(id+"F0.imprint","IMPRINT",FACE,{"disambiguationData":[TD([[makeQuery(id+"F0.imprint","IMPRINT",EDGE,{"derivedFrom":sQuery(id+"F0.wireOp",EDGE,"E12.bottom")}),-1.0]])]});
            extrude(context, id + "F3", {"entities" : qUnion([Q0, Q1, Q2, Q3, Q4]), "operationType" : NewBodyOperationType.REMOVE, "oppositeDirection" : true, "depth" : 7.62 * mm, "offsetDistance" : 25.4 * mm});
        }
        {
            var Q0;
            Q0=sQuery(id+"F0.wireOp",VERTEX,"E15.center");
            var Q1;
            Q1=makeQuery(id+"F1.opExtrude","SWEPT_BODY",BODY,{"disambiguationData":[OSD([sQuery(id+"F0.wireOp",EDGE,"E0.bottom"),sQuery(id+"F0.wireOp",EDGE,"E0.top"),sQuery(id+"F0.wireOp",EDGE,"E0.left"),sQuery(id+"F0.wireOp",EDGE,"E0.right"),sQuery(id+"F0.wireOp",EDGE,"E2.top"),sQuery(id+"F0.wireOp",EDGE,"E3.top"),sQuery(id+"F0.wireOp",EDGE,"E8.top"),sQuery(id+"F0.wireOp",EDGE,"E8.left"),sQuery(id+"F0.wireOp",EDGE,"E8.right"),sQuery(id+"F0.wireOp",EDGE,"E9.top"),sQuery(id+"F0.wireOp",EDGE,"E9.left"),sQuery(id+"F0.wireOp",EDGE,"E9.right")])]});
            hole(context, id + "F4", {"style" : HoleStyle.SIMPLE, "endStyle" : HoleEndStyle.THROUGH, "holeDiameter" : 6.35 * mm, "majorDiameter" : 6.35 * mm, "isTappedThrough" : true, "tappedDepth" : 12.7 * mm, "tapClearance" : 3, "locations" : qUnion([Q0]), "scope" : qUnion([Q1])});
        }
        {
            var Q0;
            Q0=sQuery(id+"F0.wireOp",VERTEX,"E16.center");
            var Q1;
            Q1=sQuery(id+"F0.wireOp",VERTEX,"E13.center");
            var Q2;
            Q2=sQuery(id+"F0.wireOp",VERTEX,"E14.center");
            var Q3;
            Q3=makeQuery(id+"F1.opExtrude","SWEPT_BODY",BODY,{"disambiguationData":[OSD([sQuery(id+"F0.wireOp",EDGE,"E0.bottom"),sQuery(id+"F0.wireOp",EDGE,"E0.top"),sQuery(id+"F0.wireOp",EDGE,"E0.left"),sQuery(id+"F0.wireOp",EDGE,"E0.right"),sQuery(id+"F0.wireOp",EDGE,"E2.top"),sQuery(id+"F0.wireOp",EDGE,"E3.top"),sQuery(id+"F0.wireOp",EDGE,"E8.top"),sQuery(id+"F0.wireOp",EDGE,"E8.left"),sQuery(id+"F0.wireOp",EDGE,"E8.right"),sQuery(id+"F0.wireOp",EDGE,"E9.top"),sQuery(id+"F0.wireOp",EDGE,"E9.left"),sQuery(id+"F0.wireOp",EDGE,"E9.right")])]});
            hole(context, id + "F5", {"style" : HoleStyle.SIMPLE, "endStyle" : HoleEndStyle.THROUGH, "holeDiameter" : 6.35 * mm, "majorDiameter" : 6.35 * mm, "isTappedThrough" : true, "tappedDepth" : 12.7 * mm, "tapClearance" : 3, "locations" : qUnion([Q0, Q1, Q2]), "scope" : qUnion([Q3])});
        }
        {
            var Q0;
            Q0=makeQuery(id+"F1.opExtrude","SWEPT_EDGE",EDGE,{"disambiguationData":[OSD([sQuery(id+"F0.wireOp",EDGE,"E0.bottom"),sQuery(id+"F0.wireOp",EDGE,"E0.left")])]});
            var Q1;
            Q1=makeQuery(id+"F1.opExtrude","SWEPT_EDGE",EDGE,{"disambiguationData":[OSD([sQuery(id+"F0.wireOp",EDGE,"E0.top"),sQuery(id+"F0.wireOp",EDGE,"E0.left")])]});
            var Q2;
            Q2=makeQuery(id+"F1.opExtrude","SWEPT_EDGE",EDGE,{"disambiguationData":[OSD([sQuery(id+"F0.wireOp",EDGE,"E0.bottom"),sQuery(id+"F0.wireOp",EDGE,"E0.right")])]});
            var Q3;
            Q3=makeQuery(id+"F1.opExtrude","SWEPT_EDGE",EDGE,{"disambiguationData":[OSD([sQuery(id+"F0.wireOp",EDGE,"E0.top"),sQuery(id+"F0.wireOp",EDGE,"E0.right")])]});
            fillet(context, id + "F6", {"entities" : qUnion([Q0, Q1, Q2, Q3]), "radius" : 2.03 * mm, "tangentPropagation" : true, "allowEdgeOverflow" : false});
        }
    });
